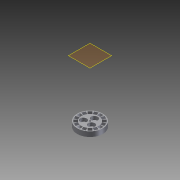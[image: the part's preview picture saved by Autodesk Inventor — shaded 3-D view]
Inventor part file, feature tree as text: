
AUTODESK INVENTOR PART (.ipt)
format: ipt  version: 2012 (Build 160160000, 160)  size: 1,379,840 bytes
history: native  units: mm
features: projected_geometry x9, extrude x6, sketch x6, other x1, plane x1, fillet x1
ambient origin geometry x8: Origin, YZ Plane, XZ Plane, XY Plane, X Axis, Y Axis, Z Axis, Center Point
bodies: Solid1 (feature_tree)
feature tree (24):
  other  "BOTTOM"
  extrude  "Extrusion1"  Depth=4.0mm TaperAngle=0.0deg
  sketch  "Sketch4"  dims[d1=4.0mm d2=0.0mm d6=4.0mm d7=0.0mm]
  plane  "Work Plane1"
  extrude  "Extrusion3"  Depth=7.0mm
  extrude  "Extrusion4"  Depth=7.0mm
  extrude  "Extrusion5"  Depth=0.4mm
  fillet  "Fillet1"  Radius=4.75mm
  extrude  "Extrusion7"  Depth=1.8mm
  extrude  "Extrusion8"  [1 undecoded]
  sketch  "Sketch5"  dims[d17=2.0mm d18=0.0mm d19=7.0mm]
  projected_geometry  "Projected Loop1"
  projected_geometry  "Projected Loop2"
  projected_geometry  "Projected Loop3"
  projected_geometry  "Projected Loop4"
  sketch  "Sketch6"  dims[d20=7.0mm d21=7.0mm]
  sketch  "Sketch7"  dims[d22=2.5mm d23=0.0mm d24=0.4mm d25=4.75mm]
  projected_geometry  "Projected Loop5"
  projected_geometry  "Projected Loop6"
  sketch  "Sketch10"  dims[d28=1.0mm d29=0.0mm d30=1.8mm]
  projected_geometry  "Projected Loop7"
  sketch  "Sketch11"  dims[d31=3.5mm d32=0.0mm]
  projected_geometry  "Projected Loop8"
  projected_geometry  "Projected Loop9"
note: 1 required parameter value undecoded (feature->parameter linkage not recoverable at this tier; creation-order binding heuristic only, values carry confidence <= 0.55)
